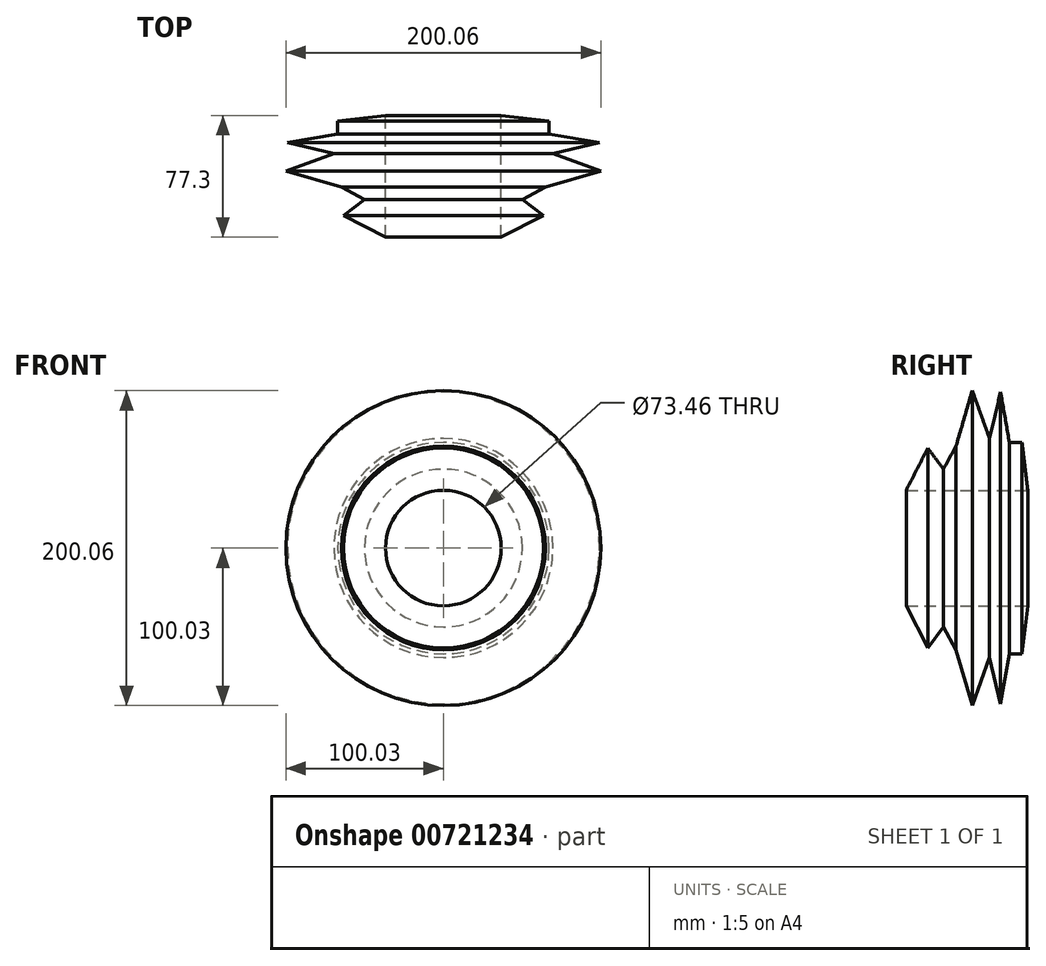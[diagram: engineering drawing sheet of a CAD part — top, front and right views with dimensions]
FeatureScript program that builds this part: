
annotation { "Feature Type Name" : "Feature", "Feature Type Description" : "" }
export const myFeature = defineFeature(function(context is Context, id is Id, definition is map)
    precondition{}
    {
        {
            var Q0;
            Q0=qCreatedBy(makeId("Top.planeOp"),FACE);
            var sketch = newSketch(context, id + "F0", { "sketchPlane" : qUnion([Q0])});
            skPoint(sketch, "E0.middle", {"position": v(0, 0) * mm});
            skLineSegment(sketch, "E1", {"start": v(36.73, 38.87) * mm, "end": v(36.73, -38.43) * mm});
            skLineSegment(sketch, "E2", {"start": v(36.73, -38.43) * mm, "end": v(63.5, -24.74) * mm});
            skLineSegment(sketch, "E3", {"start": v(63.5, -24.74) * mm, "end": v(50.12, -14.7) * mm});
            skLineSegment(sketch, "E4", {"start": v(50.12, -14.7) * mm, "end": v(64.73, -6.78) * mm});
            skLineSegment(sketch, "E5", {"start": v(64.73, -6.78) * mm, "end": v(100.03, 3.57) * mm});
            skLineSegment(sketch, "E6", {"start": v(100.03, 3.57) * mm, "end": v(69.6, 14.52) * mm});
            skLineSegment(sketch, "E7", {"start": v(69.6, 14.52) * mm, "end": v(99.11, 21.52) * mm});
            skLineSegment(sketch, "E8", {"start": v(99.11, 21.52) * mm, "end": v(67.16, 27.1) * mm});
            skLineSegment(sketch, "E9", {"start": v(67.16, 27.1) * mm, "end": v(67.16, 35.22) * mm});
            skLineSegment(sketch, "E10", {"start": v(36.73, 38.87) * mm, "end": v(67.16, 35.22) * mm});
            skLineSegment(sketch, "E11", {"start": v(0, 25.98) * mm, "end": v(0, -25.24) * mm});
            skSolve(sketch);
        }
        {
            var Q0;
            Q0=makeQuery(id+"F0.imprint","IMPRINT",FACE,{"disambiguationData":[TD([[makeQuery(id+"F0.imprint","IMPRINT",EDGE,{"derivedFrom":sQuery(id+"F0.wireOp",EDGE,"E1")}),1.0]])]});
            var Q1;
            Q1=sQuery(id+"F0.wireOp",EDGE,"E11");
            revolve(context, id + "F1", {"surfaceOperationType" : NewSurfaceOperationType.NEW, "entities" : qUnion([Q0]), "axis" : qUnion([Q1]), "revolveType" : RevolveType.FULL});
        }
    });
